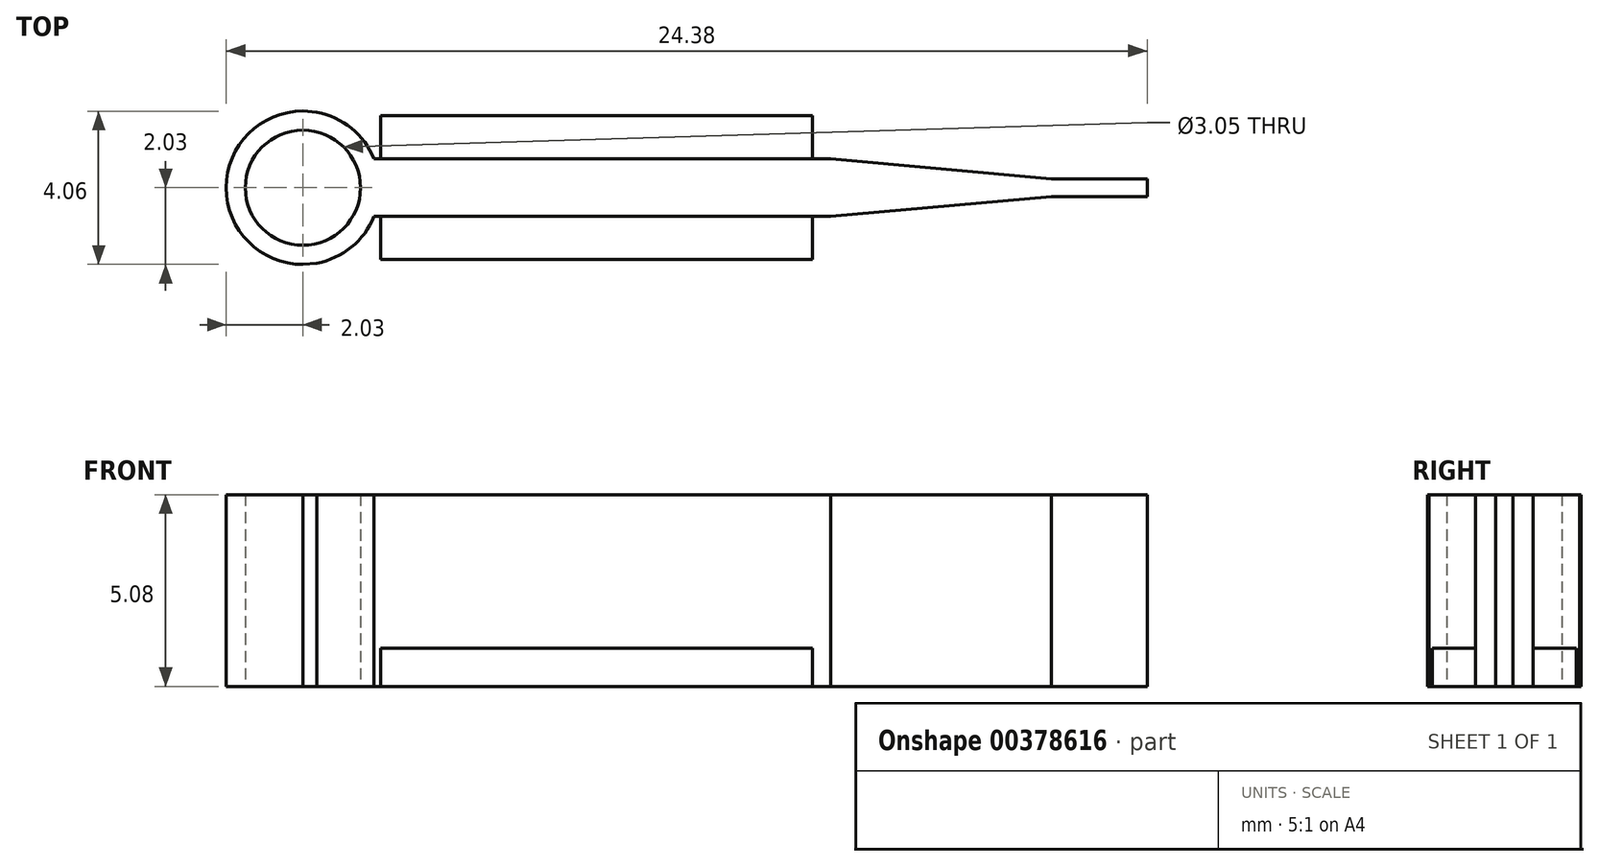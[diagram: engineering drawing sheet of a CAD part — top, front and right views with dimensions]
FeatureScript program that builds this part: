
annotation { "Feature Type Name" : "Feature", "Feature Type Description" : "" }
export const myFeature = defineFeature(function(context is Context, id is Id, definition is map)
    precondition{}
    {
        {
            var Q0;
            Q0=qCreatedBy(makeId("Top.planeOp"),FACE);
            var sketch = newSketch(context, id + "F0", { "sketchPlane" : qUnion([Q0])});
            skCircle(sketch, "E0", {"center": v(0, 0) * mm, "radius": 1.52 * mm});
            skLineSegment(sketch, "E1", {"start": v(0, 1.52) * mm, "end": v(0, -1.52) * mm});
            skLineSegment(sketch, "E2", {"start": v(0, 0) * mm, "end": v(22.35, 0) * mm});
            skLineSegment(sketch, "E3", {"start": v(0, 2.03) * mm, "end": v(0, -2.03) * mm});
            skLineSegment(sketch, "E4", {"start": v(0, 2.03) * mm, "end": v(22.35, 0) * mm});
            skLineSegment(sketch, "E5", {"start": v(22.35, 0) * mm, "end": v(0, -2.03) * mm});
            skArc(sketch, "E6", {"start": v(0, 2.03) * mm, "mid": v(-2.03, 0) * mm, "end": v(0, -2.03) * mm});
            skLineSegment(sketch, "E7", {"start": v(0.45, 2) * mm, "end": v(0.45, -2) * mm});
            skPoint(sketch, "E8.endSnap0", {"position": v(11.18, -1.02) * mm});
            skLineSegment(sketch, "E9", {"start": v(13.97, 0.76) * mm, "end": v(0.45, 0.76) * mm});
            skLineSegment(sketch, "E10", {"start": v(13.97, -0.76) * mm, "end": v(0.45, -0.76) * mm});
            skLineSegment(sketch, "E11", {"start": v(13.97, 0.76) * mm, "end": v(13.97, -0.76) * mm});
            skLineSegment(sketch, "E12", {"start": v(13.97, 0.76) * mm, "end": v(19.81, 0.76) * mm});
            skLineSegment(sketch, "E13", {"start": v(19.81, 0.76) * mm, "end": v(19.81, -0.74) * mm});
            skLineSegment(sketch, "E14", {"start": v(19.81, -0.74) * mm, "end": v(13.97, -0.76) * mm});
            skCircle(sketch, "E15", {"center": v(0, 0) * mm, "radius": 2.03 * mm});
            skLineSegment(sketch, "E16.bottom", {"start": v(19.81, 0.23) * mm, "end": v(22.35, 0.23) * mm});
            skLineSegment(sketch, "E16.top", {"start": v(19.81, -0.23) * mm, "end": v(22.35, -0.23) * mm});
            skLineSegment(sketch, "E16.left", {"start": v(19.81, 0.23) * mm, "end": v(19.81, -0.23) * mm});
            skLineSegment(sketch, "E16.right", {"start": v(22.35, 0.23) * mm, "end": v(22.35, -0.23) * mm});
            skSolve(sketch);
        }
        {
            var Q0;
            {var subQ0=sQuery(id+"F0.wireOp",EDGE,"E2");var subQ1=sQuery(id+"F0.wireOp",EDGE,"E0");var subQ2=makeQuery(id+"F0.imprint","INTERSECT",VERTEX,{"derivedFrom":[subQ1,subQ0]});Q0=makeQuery(id+"F0.imprint","IMPRINT",FACE,{"disambiguationData":[TD([[makeQuery(id+"F0.imprint","IMPRINT",EDGE,{"disambiguationData":[TD([[subQ2,1.0]])],"derivedFrom":subQ1}),-1.0]])]});}
            var Q1;
            {var subQ0=sQuery(id+"F0.wireOp",EDGE,"E9");var subQ1=sQuery(id+"F0.wireOp",EDGE,"E0");var subQ2=makeQuery(id+"F0.imprint","INTERSECT",VERTEX,{"derivedFrom":[subQ1,subQ0]});Q1=makeQuery(id+"F0.imprint","IMPRINT",FACE,{"disambiguationData":[TD([[makeQuery(id+"F0.imprint","IMPRINT",EDGE,{"disambiguationData":[TD([[subQ2,1.0]])],"derivedFrom":subQ1}),-1.0]])]});}
            var Q2;
            {var subQ0=sQuery(id+"F0.wireOp",EDGE,"E11");var subQ1=sQuery(id+"F0.wireOp",EDGE,"E2");var subQ2=makeQuery(id+"F0.imprint","INTERSECT",VERTEX,{"derivedFrom":[subQ1,subQ0]});Q2=makeQuery(id+"F0.imprint","IMPRINT",FACE,{"disambiguationData":[TD([[makeQuery(id+"F0.imprint","IMPRINT",EDGE,{"disambiguationData":[TD([[subQ2,-1.0]])],"derivedFrom":subQ1}),1.0]])]});}
            var Q3;
            {var subQ0=sQuery(id+"F0.wireOp",EDGE,"E11");var subQ1=sQuery(id+"F0.wireOp",EDGE,"E2");var subQ2=makeQuery(id+"F0.imprint","INTERSECT",VERTEX,{"derivedFrom":[subQ1,subQ0]});Q3=makeQuery(id+"F0.imprint","IMPRINT",FACE,{"disambiguationData":[TD([[makeQuery(id+"F0.imprint","IMPRINT",EDGE,{"disambiguationData":[TD([[subQ2,-1.0]])],"derivedFrom":subQ1}),-1.0]])]});}
            var Q4;
            {var subQ0=sQuery(id+"F0.wireOp",EDGE,"E4");var subQ3=sQuery(id+"F0.wireOp",EDGE,"E13");var subQ5=makeQuery(id+"F0.imprint","INTERSECT",VERTEX,{"derivedFrom":[subQ0,subQ3]});Q4=makeQuery(id+"F0.imprint","IMPRINT",FACE,{"disambiguationData":[TD([[makeQuery(id+"F0.imprint","IMPRINT",EDGE,{"disambiguationData":[TD([[subQ5,-1.0]])],"derivedFrom":subQ3}),1.0]])]});}
            var Q5;
            {var subQ0=sQuery(id+"F0.wireOp",EDGE,"E5");var subQ3=sQuery(id+"F0.wireOp",EDGE,"E13");var subQ5=makeQuery(id+"F0.imprint","INTERSECT",VERTEX,{"derivedFrom":[subQ0,subQ3]});Q5=makeQuery(id+"F0.imprint","IMPRINT",FACE,{"disambiguationData":[TD([[makeQuery(id+"F0.imprint","IMPRINT",EDGE,{"disambiguationData":[TD([[subQ5,1.0]])],"derivedFrom":subQ3}),1.0]])]});}
            var Q6;
            {var subQ4=sQuery(id+"F0.wireOp",EDGE,"E6");Q6=makeQuery(id+"F0.imprint","IMPRINT",FACE,{"disambiguationData":[TD([[makeQuery(id+"F0.imprint","IMPRINT",EDGE,{"derivedFrom":subQ4}),1.0]])]});}
            var Q7;
            {var subQ0=sQuery(id+"F0.wireOp",EDGE,"E3");var subQ1=sQuery(id+"F0.wireOp",EDGE,"E0");var subQ2=makeQuery(id+"F0.imprint","INTERSECT",VERTEX,{"disambiguationData":[OD(1.0)],"derivedFrom":[subQ1,subQ0]});Q7=makeQuery(id+"F0.imprint","IMPRINT",FACE,{"disambiguationData":[TD([[makeQuery(id+"F0.imprint","IMPRINT",EDGE,{"disambiguationData":[TD([[subQ2,-1.0]])],"derivedFrom":subQ1}),-1.0]])]});}
            var Q8;
            {var subQ0=sQuery(id+"F0.wireOp",EDGE,"E7");var subQ1=sQuery(id+"F0.wireOp",EDGE,"E0");var subQ2=makeQuery(id+"F0.imprint","INTERSECT",VERTEX,{"disambiguationData":[OD(0.0)],"derivedFrom":[subQ1,subQ0]});Q8=makeQuery(id+"F0.imprint","IMPRINT",FACE,{"disambiguationData":[TD([[makeQuery(id+"F0.imprint","IMPRINT",EDGE,{"disambiguationData":[TD([[subQ2,-1.0]])],"derivedFrom":subQ1}),-1.0]])]});}
            var Q9;
            {var subQ0=sQuery(id+"F0.wireOp",EDGE,"E9");var subQ1=sQuery(id+"F0.wireOp",EDGE,"E0");var subQ2=makeQuery(id+"F0.imprint","INTERSECT",VERTEX,{"derivedFrom":[subQ1,subQ0]});Q9=makeQuery(id+"F0.imprint","IMPRINT",FACE,{"disambiguationData":[TD([[makeQuery(id+"F0.imprint","IMPRINT",EDGE,{"disambiguationData":[TD([[subQ2,-1.0]])],"derivedFrom":subQ1}),-1.0]])]});}
            var Q10;
            {var subQ0=sQuery(id+"F0.wireOp",EDGE,"E7");var subQ1=sQuery(id+"F0.wireOp",EDGE,"E0");var subQ2=makeQuery(id+"F0.imprint","INTERSECT",VERTEX,{"disambiguationData":[OD(1.0)],"derivedFrom":[subQ1,subQ0]});Q10=makeQuery(id+"F0.imprint","IMPRINT",FACE,{"disambiguationData":[TD([[makeQuery(id+"F0.imprint","IMPRINT",EDGE,{"disambiguationData":[TD([[subQ2,-1.0]])],"derivedFrom":subQ1}),-1.0]])]});}
            var Q11;
            {var subQ0=sQuery(id+"F0.wireOp",EDGE,"E3");var subQ1=sQuery(id+"F0.wireOp",EDGE,"E0");var subQ2=makeQuery(id+"F0.imprint","INTERSECT",VERTEX,{"disambiguationData":[OD(0.0)],"derivedFrom":[subQ1,subQ0]});Q11=makeQuery(id+"F0.imprint","IMPRINT",FACE,{"disambiguationData":[TD([[makeQuery(id+"F0.imprint","IMPRINT",EDGE,{"disambiguationData":[TD([[subQ2,-1.0]])],"derivedFrom":subQ1}),-1.0]])]});}
            var Q12;
            {var subQ0=sQuery(id+"F0.wireOp",EDGE,"E15");var subQ1=sQuery(id+"F0.wireOp",EDGE,"E2");var subQ2=makeQuery(id+"F0.imprint","INTERSECT",VERTEX,{"derivedFrom":[subQ1,subQ0]});Q12=makeQuery(id+"F0.imprint","IMPRINT",FACE,{"disambiguationData":[TD([[makeQuery(id+"F0.imprint","IMPRINT",EDGE,{"disambiguationData":[TD([[subQ2,-1.0]])],"derivedFrom":subQ1}),1.0]])]});}
            var Q13;
            {var subQ0=sQuery(id+"F0.wireOp",EDGE,"E15");var subQ1=sQuery(id+"F0.wireOp",EDGE,"E2");var subQ2=makeQuery(id+"F0.imprint","INTERSECT",VERTEX,{"derivedFrom":[subQ1,subQ0]});Q13=makeQuery(id+"F0.imprint","IMPRINT",FACE,{"disambiguationData":[TD([[makeQuery(id+"F0.imprint","IMPRINT",EDGE,{"disambiguationData":[TD([[subQ2,-1.0]])],"derivedFrom":subQ1}),-1.0]])]});}
            var Q14;
            {var subQ1=sQuery(id+"F0.wireOp",EDGE,"E2");var subQ3=sQuery(id+"F0.wireOp",EDGE,"E16.left");var subQ4=makeQuery(id+"F0.imprint","INTERSECT",VERTEX,{"derivedFrom":[subQ1,subQ3]});Q14=makeQuery(id+"F0.imprint","IMPRINT",FACE,{"disambiguationData":[TD([[makeQuery(id+"F0.imprint","IMPRINT",EDGE,{"disambiguationData":[TD([[subQ4,-1.0]])],"derivedFrom":subQ1}),-1.0]])]});}
            var Q15;
            {var subQ1=sQuery(id+"F0.wireOp",EDGE,"E2");var subQ3=sQuery(id+"F0.wireOp",EDGE,"E16.left");var subQ4=makeQuery(id+"F0.imprint","INTERSECT",VERTEX,{"derivedFrom":[subQ1,subQ3]});Q15=makeQuery(id+"F0.imprint","IMPRINT",FACE,{"disambiguationData":[TD([[makeQuery(id+"F0.imprint","IMPRINT",EDGE,{"disambiguationData":[TD([[subQ4,-1.0]])],"derivedFrom":subQ1}),1.0]])]});}
            var Q16;
            {var subQ3=sQuery(id+"F0.wireOp",EDGE,"E16.bottom");Q16=makeQuery(id+"F0.imprint","IMPRINT",FACE,{"disambiguationData":[TD([[makeQuery(id+"F0.imprint","IMPRINT",EDGE,{"derivedFrom":subQ3}),-1.0]])]});}
            var Q17;
            {var subQ3=sQuery(id+"F0.wireOp",EDGE,"E16.top");Q17=makeQuery(id+"F0.imprint","IMPRINT",FACE,{"disambiguationData":[TD([[makeQuery(id+"F0.imprint","IMPRINT",EDGE,{"derivedFrom":subQ3}),1.0]])]});}
            extrude(context, id + "F1", {"entities" : qUnion([Q0, Q1, Q2, Q3, Q4, Q5, Q6, Q7, Q8, Q9, Q10, Q11, Q12, Q13, Q14, Q15, Q16, Q17]), "depth" : 5.08 * mm});
        }
        {
            var Q0;
            {var subQ3=sQuery(id+"F0.wireOp",EDGE,"E0");var subQ7=sQuery(id+"F0.wireOp",EDGE,"E2");var subQ8=makeQuery(id+"F0.imprint","INTERSECT",VERTEX,{"derivedFrom":[subQ3,subQ7]});Q0=makeQuery(id+"F0.imprint","IMPRINT",FACE,{"disambiguationData":[TD([[makeQuery(id+"F0.imprint","IMPRINT",EDGE,{"disambiguationData":[TD([[subQ8,1.0]])],"derivedFrom":subQ3}),-1.0]])]});}
            var Q1;
            {var subQ1=sQuery(id+"F0.wireOp",EDGE,"E3");var subQ5=sQuery(id+"F0.wireOp",EDGE,"E0");var subQ6=makeQuery(id+"F0.imprint","INTERSECT",VERTEX,{"disambiguationData":[OD(0.0)],"derivedFrom":[subQ5,subQ1]});Q1=makeQuery(id+"F0.imprint","IMPRINT",FACE,{"disambiguationData":[TD([[makeQuery(id+"F0.imprint","IMPRINT",EDGE,{"disambiguationData":[TD([[subQ6,1.0]])],"derivedFrom":subQ5}),-1.0]])]});}
            var Q2;
            {var subQ4=sQuery(id+"F0.wireOp",EDGE,"E6");Q2=makeQuery(id+"F0.imprint","IMPRINT",FACE,{"disambiguationData":[TD([[makeQuery(id+"F0.imprint","IMPRINT",EDGE,{"derivedFrom":subQ4}),1.0]])]});}
            extrude(context, id + "F2", {"entities" : qUnion([Q0, Q1, Q2]), "operationType" : NewBodyOperationType.ADD, "depth" : 5.03 * mm});
        }
        {
            var Q0;
            Q0=qCreatedBy(makeId("Top.planeOp"),FACE);
            var sketch = newSketch(context, id + "F3", { "sketchPlane" : qUnion([Q0])});
            skLineSegment(sketch, "E17.bottom", {"start": v(2.06, 1.9) * mm, "end": v(13.49, 1.9) * mm});
            skLineSegment(sketch, "E17.top", {"start": v(2.06, -1.9) * mm, "end": v(13.49, -1.9) * mm});
            skLineSegment(sketch, "E17.left", {"start": v(2.06, 1.9) * mm, "end": v(2.06, -1.9) * mm});
            skLineSegment(sketch, "E17.right", {"start": v(13.49, 1.9) * mm, "end": v(13.49, -1.9) * mm});
            skPoint(sketch, "E17.middle", {"position": v(7.77, 0) * mm});
            skSolve(sketch);
        }
        {
            var Q0;
            Q0 = qSketchRegion(id + "F3", true);
            extrude(context, id + "F4", {"entities" : qUnion([Q0]), "operationType" : NewBodyOperationType.ADD, "depth" : 1.02 * mm});
        }
    });
